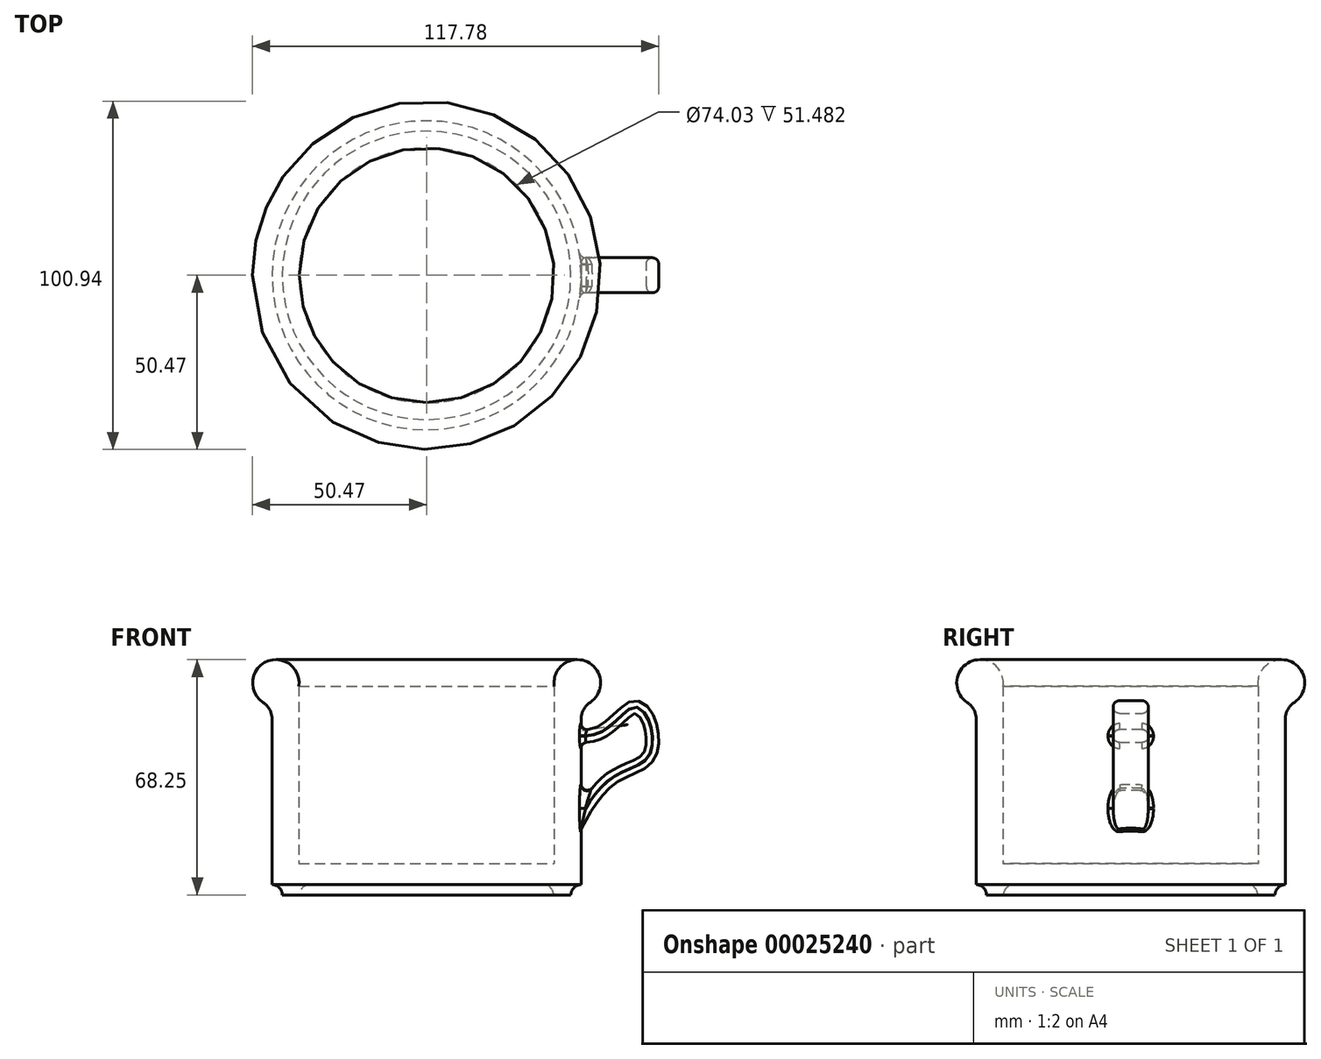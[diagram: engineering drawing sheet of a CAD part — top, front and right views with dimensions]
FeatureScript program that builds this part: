
annotation { "Feature Type Name" : "Feature", "Feature Type Description" : "" }
export const myFeature = defineFeature(function(context is Context, id is Id, definition is map)
    precondition{}
    {
        {
            var Q0;
            Q0=qCreatedBy(makeId("Front.planeOp"),FACE);
            var sketch = newSketch(context, id + "F0", { "sketchPlane" : qUnion([Q0])});
            skLineSegment(sketch, "E0", {"start": v(-44.81, 50.93) * mm, "end": v(-44.81, 2.97) * mm});
            skArc(sketch, "E1", {"start": v(-41.84, 0) * mm, "mid": v(-42.71, 2.1) * mm, "end": v(-44.81, 2.97) * mm});
            skLineSegment(sketch, "E2", {"start": v(-41.84, 0) * mm, "end": v(-36.82, 0) * mm});
            skArc(sketch, "E3", {"start": v(-33.84, 2.98) * mm, "mid": v(-35.95, 2.1) * mm, "end": v(-36.82, 0) * mm});
            skLineSegment(sketch, "E4", {"start": v(-33.84, 2.98) * mm, "end": v(0, 2.98) * mm});
            skLineSegment(sketch, "E5", {"start": v(0, 2.98) * mm, "end": v(0, 9.1) * mm});
            skLineSegment(sketch, "E6", {"start": v(0, 9.1) * mm, "end": v(-37.02, 9.1) * mm});
            skLineSegment(sketch, "E7", {"start": v(-37.02, 9.1) * mm, "end": v(-37.02, 60.58) * mm});
            skArc(sketch, "E8", {"start": v(-44.81, 50.93) * mm, "mid": v(-45.52, 53.74) * mm, "end": v(-47.46, 55.88) * mm});
            skArc(sketch, "E9", {"start": v(-47.46, 55.88) * mm, "mid": v(-46.49, 67.66) * mm, "end": v(-37.02, 60.58) * mm});
            skSolve(sketch);
        }
        {
            var Q0;
            Q0 = qSketchRegion(id + "F0", true);
            var Q1;
            Q1=sQuery(id+"F0.wireOp",EDGE,"E5");
            revolve(context, id + "F1", {"entities" : qUnion([Q0]), "axis" : qUnion([Q1]), "revolveType" : RevolveType.FULL});
        }
        {
            var Q0;
            Q0=qCreatedBy(makeId("Front.planeOp"),FACE);
            var sketch = newSketch(context, id + "F2", { "sketchPlane" : qUnion([Q0])});
            skFitSpline(sketch, "E10", {"points": [v(40.08, 10.13) * mm, v(53.1, 31.1) * mm, v(65.7, 38.8) * mm, v(65.52, 52.56) * mm, v(59.26, 56.14) * mm, v(48.97, 48.54) * mm, v(39.7, 49.8) * mm], "startDerivative": vector(38.55, 55.38) * mm, "endDerivative": vector(-29.92, 34.65) * mm});
            skLineSegment(sketch, "E11", {"start": v(39.7, 49.8) * mm, "end": v(40.08, 10.13) * mm});
            skLineSegment(sketch, "E12.0", {"start": v(43.4, 44.38) * mm, "end": v(43.59, 24.38) * mm});
            skFitSpline(sketch, "E12.1", {"points": [v(37.09, 12.21) * mm, v(37.23, 12.42) * mm, v(37.56, 12.93) * mm, v(38.35, 14.31) * mm, v(39.5, 16.54) * mm, v(41.1, 19.73) * mm, v(42.9, 23.2) * mm, v(44.58, 26.13) * mm, v(46.05, 28.4) * mm, v(47.23, 30.06) * mm, v(48.5, 31.63) * mm, v(49.63, 32.85) * mm, v(50.6, 33.76) * mm, v(51.6, 34.61) * mm, v(52.87, 35.53) * mm, v(54.39, 36.45) * mm, v(56.34, 37.46) * mm, v(58.58, 38.42) * mm, v(60.38, 39.21) * mm, v(61.46, 39.8) * mm, v(61.96, 40.15) * mm, v(62.28, 40.42) * mm, v(62.47, 40.6) * mm, v(62.64, 40.8) * mm, v(62.78, 40.98) * mm, v(62.92, 41.22) * mm, v(63.1, 41.6) * mm, v(63.32, 42.18) * mm, v(63.52, 43.04) * mm, v(63.69, 44.35) * mm, v(63.67, 46.2) * mm, v(63.35, 48.06) * mm, v(62.94, 49.4) * mm, v(62.64, 50.17) * mm, v(62.39, 50.7) * mm, v(62.12, 51.18) * mm, v(61.78, 51.69) * mm, v(61.38, 52.14) * mm, v(61.02, 52.45) * mm, v(60.74, 52.62) * mm, v(60.56, 52.68) * mm, v(60.48, 52.69) * mm, v(60.44, 52.69) * mm, v(60.39, 52.67) * mm, v(60.34, 52.66) * mm, v(60.27, 52.63) * mm, v(60.14, 52.57) * mm, v(59.84, 52.4) * mm, v(59.34, 52.05) * mm, v(58.6, 51.42) * mm, v(57.75, 50.64) * mm, v(56.81, 49.75) * mm, v(55.78, 48.79) * mm, v(54.65, 47.8) * mm, v(53.6, 46.99) * mm, v(52.7, 46.37) * mm, v(51.97, 45.93) * mm, v(51.2, 45.53) * mm, v(50.51, 45.22) * mm, v(49.95, 45) * mm, v(49.38, 44.82) * mm, v(48.67, 44.62) * mm, v(47.82, 44.44) * mm, v(46.7, 44.28) * mm, v(45.31, 44.21) * mm, v(43.71, 44.31) * mm, v(42.18, 44.57) * mm, v(40.74, 44.98) * mm, v(39.38, 45.55) * mm, v(38.1, 46.3) * mm, v(37.32, 47) * mm, v(36.94, 47.43) * mm]});
            skSolve(sketch);
        }
        {
            var Q0;
            Q0=makeQuery(id+"F2.imprint","IMPRINT",FACE,{"disambiguationData":[TD([[makeQuery(id+"F2.imprint","IMPRINT",EDGE,{"derivedFrom":sQuery(id+"F2.wireOp",EDGE,"E10")}),1.0]])]});
            extrude(context, id + "F3", {"entities" : qUnion([Q0]), "operationType" : NewBodyOperationType.ADD, "endBound" : BoundingType.SYMMETRIC, "depth" : 10.16 * mm});
        }
        {
            var Q0;
            Q0=makeQuery(id+"F3.opExtrude","CAP_EDGE",EDGE,{"disambiguationData":[OSD([sQuery(id+"F2.wireOp",EDGE,"E12.1")])],"isStart":true});
            var Q1;
            Q1=makeQuery(id+"F3.opExtrude","CAP_EDGE",EDGE,{"disambiguationData":[OSD([sQuery(id+"F2.wireOp",EDGE,"E10")])],"isStart":true});
            var Q2;
            Q2=makeQuery(id+"F3.opExtrude","CAP_EDGE",EDGE,{"disambiguationData":[OSD([sQuery(id+"F2.wireOp",EDGE,"E12.1")])],"isStart":false});
            var Q3;
            Q3=makeQuery(id+"F3.opExtrude","CAP_EDGE",EDGE,{"disambiguationData":[OSD([sQuery(id+"F2.wireOp",EDGE,"E10")])],"isStart":false});
            var Q4;
            Q4=makeQuery(id+"F3.boolean.opBoolean","INTERSECT",EDGE,{"disambiguationData":[OD(0.0)],"derivedFrom":[makeQuery(id+"F1.opRevolve","SWEPT_FACE",FACE,{"disambiguationData":[OSD([sQuery(id+"F0.wireOp",EDGE,"E0")])]}),makeQuery(id+"F3.opExtrude","SWEPT_FACE",FACE,{"disambiguationData":[OSD([sQuery(id+"F2.wireOp",EDGE,"E10")])]})]});
            var Q5;
            Q5=makeQuery(id+"F3.boolean.opBoolean","INTERSECT",EDGE,{"disambiguationData":[OD(1.0)],"derivedFrom":[makeQuery(id+"F1.opRevolve","SWEPT_FACE",FACE,{"disambiguationData":[OSD([sQuery(id+"F0.wireOp",EDGE,"E0")])]}),makeQuery(id+"F3.opExtrude","SWEPT_FACE",FACE,{"disambiguationData":[OSD([sQuery(id+"F2.wireOp",EDGE,"E12.1")])]})]});
            var Q6;
            Q6=makeQuery(id+"F3.boolean.opBoolean","INTERSECT",EDGE,{"disambiguationData":[OD(1.0)],"derivedFrom":[makeQuery(id+"F1.opRevolve","SWEPT_FACE",FACE,{"disambiguationData":[OSD([sQuery(id+"F0.wireOp",EDGE,"E0")])]}),makeQuery(id+"F3.opExtrude","SWEPT_FACE",FACE,{"disambiguationData":[OSD([sQuery(id+"F2.wireOp",EDGE,"E10")])]})]});
            var Q7;
            Q7=makeQuery(id+"F3.boolean.opBoolean","INTERSECT",EDGE,{"disambiguationData":[OD(0.0)],"derivedFrom":[makeQuery(id+"F1.opRevolve","SWEPT_FACE",FACE,{"disambiguationData":[OSD([sQuery(id+"F0.wireOp",EDGE,"E0")])]}),makeQuery(id+"F3.opExtrude","SWEPT_FACE",FACE,{"disambiguationData":[OSD([sQuery(id+"F2.wireOp",EDGE,"E12.1")])]})]});
            var Q8;
            Q8=makeQuery(id+"F3.boolean.opBoolean","INTERSECT",EDGE,{"disambiguationData":[OD(1.0)],"derivedFrom":[makeQuery(id+"F1.opRevolve","SWEPT_FACE",FACE,{"disambiguationData":[OSD([sQuery(id+"F0.wireOp",EDGE,"E0")])]}),makeQuery(id+"F3.opExtrude","CAP_FACE",FACE,{"disambiguationData":[OSD([sQuery(id+"F2.wireOp",EDGE,"E10"),sQuery(id+"F2.wireOp",EDGE,"E11"),sQuery(id+"F2.wireOp",EDGE,"E12.0"),sQuery(id+"F2.wireOp",EDGE,"E12.1")])],"isStart":false})]});
            var Q9;
            Q9=makeQuery(id+"F3.boolean.opBoolean","INTERSECT",EDGE,{"disambiguationData":[OD(1.0)],"derivedFrom":[makeQuery(id+"F1.opRevolve","SWEPT_FACE",FACE,{"disambiguationData":[OSD([sQuery(id+"F0.wireOp",EDGE,"E0")])]}),makeQuery(id+"F3.opExtrude","CAP_FACE",FACE,{"disambiguationData":[OSD([sQuery(id+"F2.wireOp",EDGE,"E10"),sQuery(id+"F2.wireOp",EDGE,"E11"),sQuery(id+"F2.wireOp",EDGE,"E12.0"),sQuery(id+"F2.wireOp",EDGE,"E12.1")])],"isStart":true})]});
            var Q10;
            Q10=makeQuery(id+"F3.boolean.opBoolean","INTERSECT",EDGE,{"disambiguationData":[OD(0.0)],"derivedFrom":[makeQuery(id+"F1.opRevolve","SWEPT_FACE",FACE,{"disambiguationData":[OSD([sQuery(id+"F0.wireOp",EDGE,"E0")])]}),makeQuery(id+"F3.opExtrude","CAP_FACE",FACE,{"disambiguationData":[OSD([sQuery(id+"F2.wireOp",EDGE,"E10"),sQuery(id+"F2.wireOp",EDGE,"E11"),sQuery(id+"F2.wireOp",EDGE,"E12.0"),sQuery(id+"F2.wireOp",EDGE,"E12.1")])],"isStart":true})]});
            fillet(context, id + "F4", {"entities" : qUnion([Q0, Q1, Q2, Q3, Q4, Q5, Q6, Q7, Q8, Q9, Q10]), "radius" : 1.78 * mm, "tangentPropagation" : true, "allowEdgeOverflow" : false});
        }
    });
